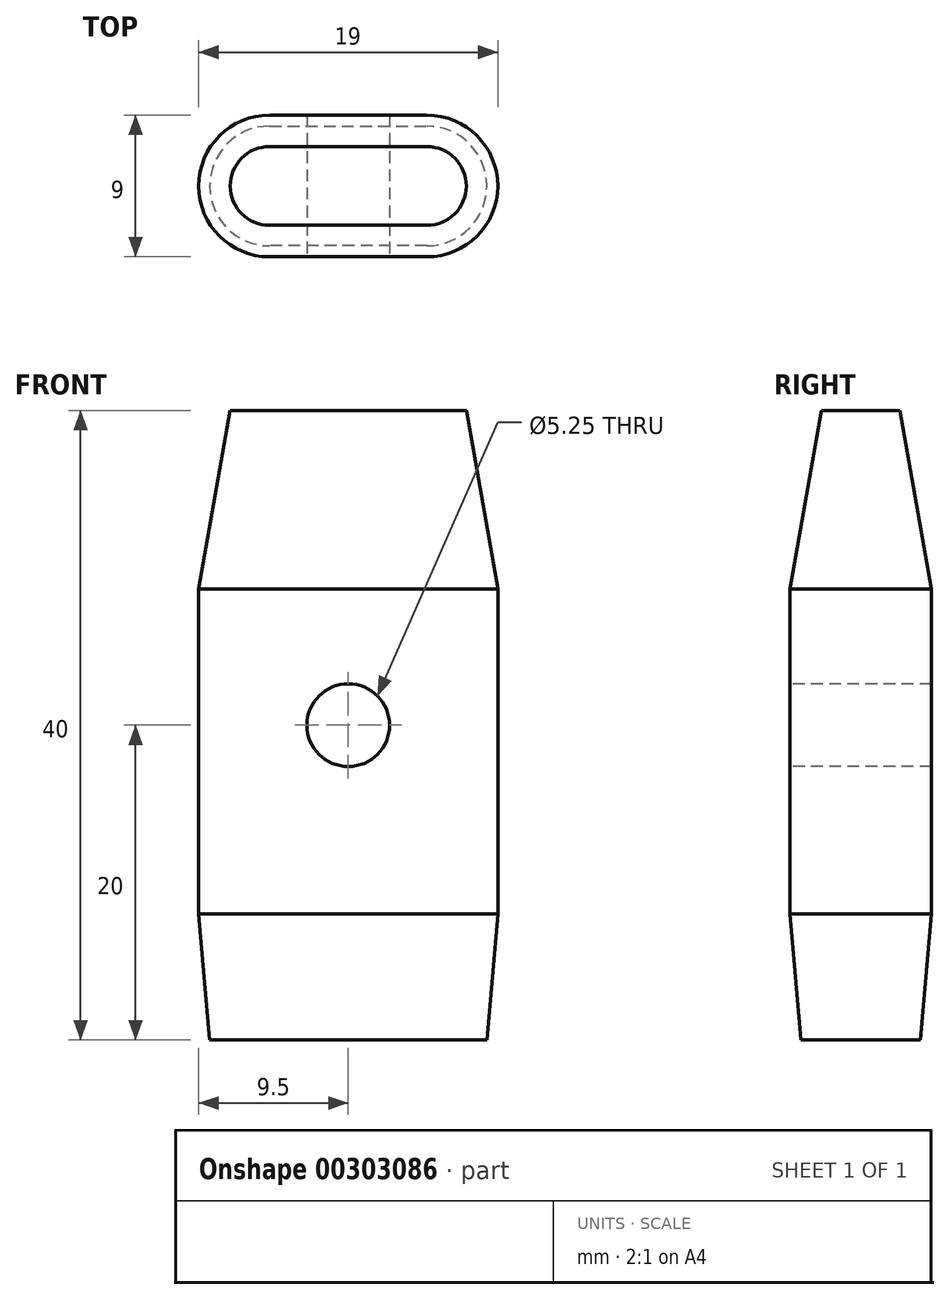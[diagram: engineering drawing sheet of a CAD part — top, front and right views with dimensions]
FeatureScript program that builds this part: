
annotation { "Feature Type Name" : "Feature", "Feature Type Description" : "" }
export const myFeature = defineFeature(function(context is Context, id is Id, definition is map)
    precondition{}
    {
        {
            var Q0;
            Q0=qCreatedBy(makeId("Top.planeOp"),FACE);
            var sketch = newSketch(context, id + "F0", { "sketchPlane" : qUnion([Q0])});
            skLineSegment(sketch, "E0", {"start": v(0, 0) * mm, "end": v(10, 0) * mm});
            skLineSegment(sketch, "E1", {"start": v(10, 0) * mm, "end": v(10, 9) * mm, "construction": true});
            skLineSegment(sketch, "E2", {"start": v(10, 9) * mm, "end": v(0, 9) * mm});
            skLineSegment(sketch, "E3", {"start": v(0, 9) * mm, "end": v(0, 0) * mm, "construction": true});
            skArc(sketch, "E4", {"start": v(0, 9) * mm, "mid": v(-4.5, 4.5) * mm, "end": v(0, 0) * mm});
            skArc(sketch, "E5", {"start": v(10, 0) * mm, "mid": v(14.5, 4.5) * mm, "end": v(10, 9) * mm});
            skSolve(sketch);
        }
        {
            var Q0;
            Q0 = qSketchRegion(id + "F0", true);
            extrude(context, id + "F1", {"entities" : qUnion([Q0]), "depth" : 40 * mm});
        }
        {
            var Q0;
            Q0=makeQuery(id+"F1.opExtrude","SWEPT_FACE",FACE,{"disambiguationData":[OSD([sQuery(id+"F0.wireOp",EDGE,"E0")])]});
            var sketch = newSketch(context, id + "F2", { "sketchPlane" : qUnion([Q0])});
            skLineSegment(sketch, "E6", {"start": v(0, 20) * mm, "end": v(10, 20) * mm, "construction": true});
            skCircle(sketch, "E7", {"center": v(5, 20) * mm, "radius": 2.62 * mm});
            skSolve(sketch);
        }
        {
            var Q0;
            Q0 = qSketchRegion(id + "F2", true);
            extrude(context, id + "F3", {"entities" : qUnion([Q0]), "operationType" : NewBodyOperationType.REMOVE, "oppositeDirection" : true, "depth" : 25 * mm});
        }
        {
            var Q0;
            Q0=makeQuery(id+"F1.opExtrude","CAP_FACE",FACE,{"disambiguationData":[OSD([sQuery(id+"F0.wireOp",EDGE,"E0"),sQuery(id+"F0.wireOp",EDGE,"E2"),sQuery(id+"F0.wireOp",EDGE,"E4"),sQuery(id+"F0.wireOp",EDGE,"E5")])],"isStart":true});
            chamfer(context, id + "F4", {"entities" : qUnion([Q0]), "chamferType" : ChamferType.OFFSET_ANGLE, "width" : 8 * mm, "oppositeDirection" : false, "angle" : 5 * degree, "tangentPropagation" : true});
        }
        {
            var Q0;
            Q0=makeQuery(id+"F1.opExtrude","CAP_FACE",FACE,{"disambiguationData":[OSD([sQuery(id+"F0.wireOp",EDGE,"E0"),sQuery(id+"F0.wireOp",EDGE,"E2"),sQuery(id+"F0.wireOp",EDGE,"E4"),sQuery(id+"F0.wireOp",EDGE,"E5")])],"isStart":false});
            chamfer(context, id + "F5", {"entities" : qUnion([Q0]), "chamferType" : ChamferType.OFFSET_ANGLE, "width" : 2 * mm, "oppositeDirection" : false, "angle" : 80 * degree, "tangentPropagation" : true});
        }
    });
